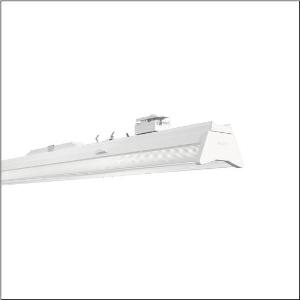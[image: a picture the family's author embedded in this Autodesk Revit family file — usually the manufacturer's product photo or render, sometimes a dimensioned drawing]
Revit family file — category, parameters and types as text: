
# Revit family: licross_r__21_performance_mo_52td16cn49xg_b518
name_source: partatom
category: Lighting Fixtures
units: mm (PartAtom-declared; Revit-internal decimal feet)

## family parameters
Cut with Voids When Loaded = No
Host = Face
Light Source = No
Part Type = Normal
Room Calculation Point = No
Round Connector Dimension = Use Diameter
Shared = No

## types (1)
- --- (1 x LED, 9240 lm, 50.4 W, 4000K)
    Apparent Load = 50 VA
    CIE Flux Codes = 66 88 96 79 100
    Color Rendering = 80
    Color Temperature = 4000K
    Default Elevation = 1800 mm
    Description = Licross® 21 Performance MO, luminaire insert, of sheet steel, galvanised, coil coated, white, length: 1.500mm, width: 120mm, height: 123mm, LED rated luminous flux: 9.240lm, light colour: 840, control gear: ON/OFF Multilumen, CLOi, control gear: ECG Multilumen, with plug, 3-pole, with phase selection, mains connection: 220..240V, AC, 50/60Hz, start of lifetime: 50W, end of service life: 61W, halogen-free wiring, primary light control with lens, of plastic, primary optical cover: cover, of PMMA, light emission: direct/indirect distribution, primary light characteristic: symmetric, protection rating (complete): IP54, insulation class (complete): insulation class I (protective earthing), certification: CE, ENEC, UKCA, protection symbol: D if used in an environment with non-conductive dust loads with corresponding accessories, impact resistance: IK06, permissible ambient temperature for indoor applications: -35..+45°C, corresponds to IFS (International Featured Standards) requirements for safety and quality in the food industry, reducing of maximum allowable ambient temperature of 5°C with ceiling mounting, LABS conformity tested according to VDMA 24364:2018-05, packaging unit: 1 piece
    Height = 114 mm
    Lamp = 1 x LED
    Lamp Light Flux = 9240 lm
    Lamp Power = 50.4 W
    Lamp count = 1
    Length = 1500 mm
    Luminous efficacy = 183 lm/W
    Manufacturer = Siteco
    ModVariant = No
    Model = 52TD16CN49XG
    Mounting Place = Ceiling
    Mounting Type = Pendant
    Number of Poles = 1
    OnlyDefault = Yes
    Power Factor = 1
    Product Name = Licross® 21 Performance MO
    Product group = luminaire insert
    ProductGroupID = 901
    Protection Class = Protection class I
    Protection Degree = IP 54
    RLX_Detail_Level = 1
    RLX_Emergency_Light_Flux = 0 lm
    RLX_Emergency_Type = 0
    RLX_Emergency_Type_DB = No
    RlxData = <blob elided: 31853 chars, md5=d37e6aa9>
    Socket = socket
    Standby Power = 0 W
    System Light Flux = 9240 lm
    System Power = 50 W
    Type Comments = factory setting: luminous flux: 100 % | (A | C | E) | 117 mA
    Type Image = l_1256138.jpg
    URL = http://relux.com
    VarID = @adj_059807
    Voltage = 0 V
    Weight = 0.00 kg
    Width = 120 mm

## geometry (parser evidence)
native form markers: Blend x4, Sweep x11
no freeform markers — native parametric forms only
